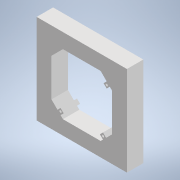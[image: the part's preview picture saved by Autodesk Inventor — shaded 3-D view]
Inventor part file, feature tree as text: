
AUTODESK INVENTOR PART (.ipt)
format: ipt  version: 2021.2 (Build 252289000, 289)  size: 221,184 bytes
history: native  units: mm
features: reference x18, other x5, extrude x3, sketch x3
ambient origin geometry x8: Origin, YZ Plane, XZ Plane, XY Plane, X Axis, Y Axis, Z Axis, Center Point
bodies: Body1 (feature_tree)
feature tree (29):
  other  "Твердое тело1"
  extrude  "Выдавливание1"  Depth=2.5mm
  extrude  "Выдавливание2"  Depth=2.0mm
  sketch  "Эскиз3"
  other  "РабПлоскость1"
  extrude  "Выдавливание3"  Depth=13.0mm TaperAngle=0.0deg
  sketch  "Эскиз1"
  reference  "Ссылка1"
  sketch  "Эскиз2"
  reference  "Ссылка2"
  reference  "Ссылка3"
  reference  "Ссылка4"
  reference  "Ссылка5"
  reference  "Ссылка6"
  reference  "Ссылка7"
  reference  "Ссылка8"
  reference  "Ссылка9"
  reference  "Ссылка10"
  reference  "Ссылка11"
  reference  "Ссылка12"
  reference  "Ссылка13"
  reference  "Ссылка14"
  reference  "Ссылка15"
  reference  "Ссылка16"
  reference  "Ссылка17"
  reference  "Ссылка18"
  parser-record x1  (decoder bookkeeping rows leaked as tree rows — omitted from the tree; the rows remain in map.json)
  other  "Сборка1.iam"
  other  "Середина:1"
note: 1 file-system path scrubbed to <path> (originals preserved in map.json)
